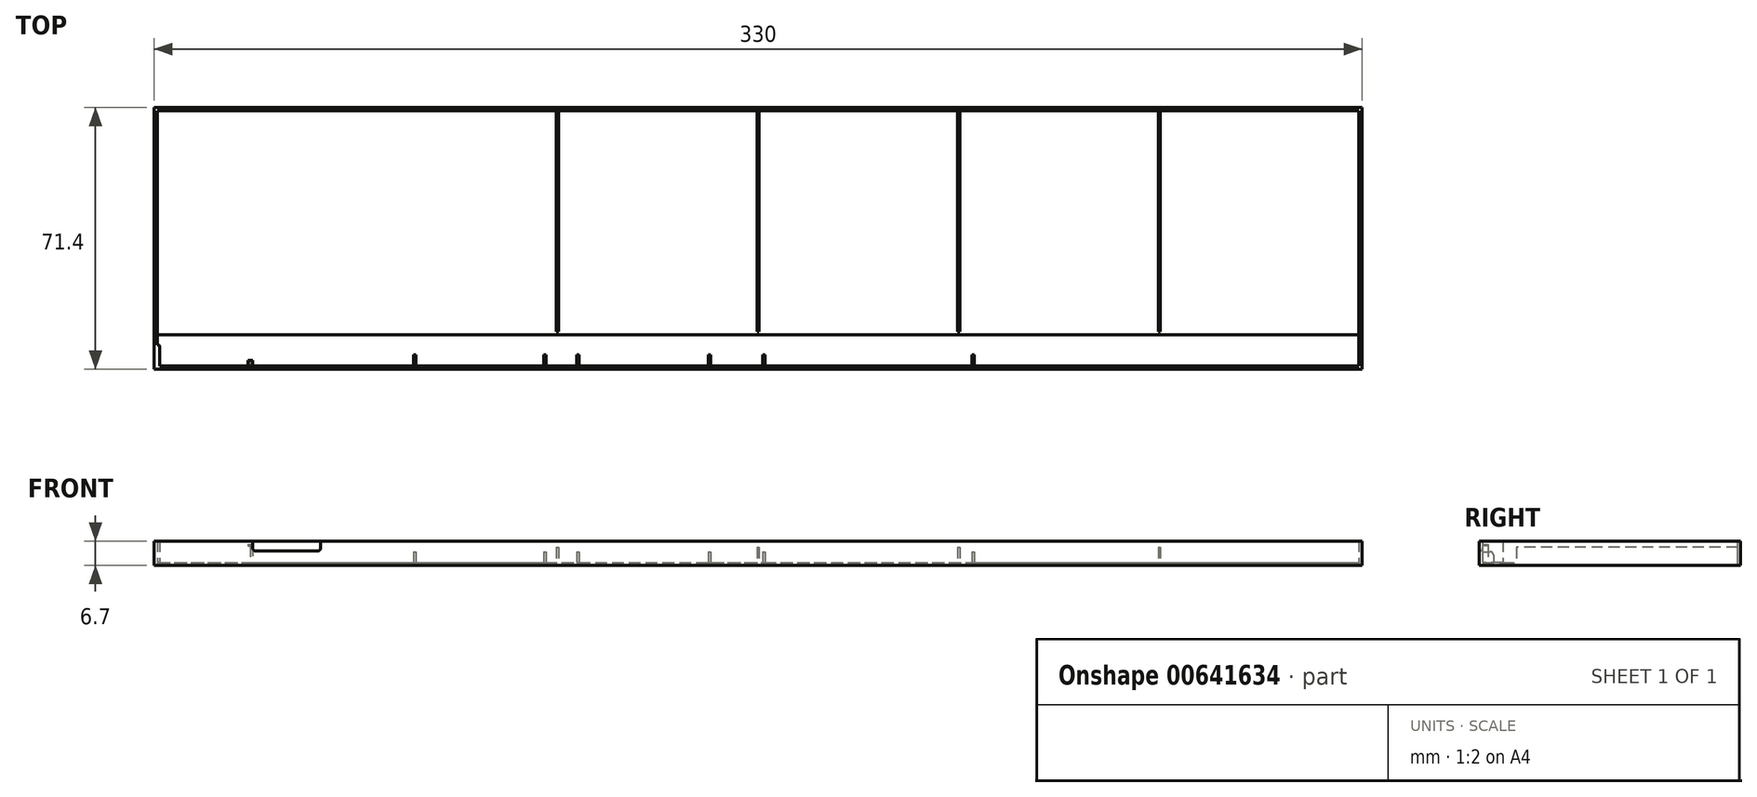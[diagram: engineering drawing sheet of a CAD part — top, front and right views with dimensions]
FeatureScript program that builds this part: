
annotation { "Feature Type Name" : "Feature", "Feature Type Description" : "" }
export const myFeature = defineFeature(function(context is Context, id is Id, definition is map)
    precondition{}
    {
        {
            var Q0;
            Q0=qCreatedBy(makeId("Top.planeOp"),FACE);
            var sketch = newSketch(context, id + "F0", { "sketchPlane" : qUnion([Q0])});
            skLineSegment(sketch, "E0.bottom", {"start": v(-165, -35.7) * mm, "end": v(165, -35.7) * mm});
            skLineSegment(sketch, "E0.top", {"start": v(-165, 35.7) * mm, "end": v(165, 35.7) * mm});
            skLineSegment(sketch, "E0.left", {"start": v(-165, -35.7) * mm, "end": v(-165, 35.7) * mm});
            skLineSegment(sketch, "E0.right", {"start": v(165, -35.7) * mm, "end": v(165, 35.7) * mm});
            skLineSegment(sketch, "E1.bottom", {"start": v(-164.1, -34.8) * mm, "end": v(164.1, -34.8) * mm});
            skLineSegment(sketch, "E1.top", {"start": v(-164.1, 34.8) * mm, "end": v(164.1, 34.8) * mm});
            skLineSegment(sketch, "E1.left", {"start": v(-164.1, -34.8) * mm, "end": v(-164.1, 34.8) * mm});
            skLineSegment(sketch, "E1.right", {"start": v(164.1, -34.8) * mm, "end": v(164.1, 34.8) * mm});
            skLineSegment(sketch, "E2", {"start": v(0, 35.7) * mm, "end": v(0, -35.7) * mm, "construction": true});
            skLineSegment(sketch, "E3", {"start": v(165, 0) * mm, "end": v(-165, 0) * mm, "construction": true});
            skPoint(sketch, "E4", {"position": v(0, 0) * mm});
            skLineSegment(sketch, "E5.bottom", {"start": v(-164.1, -26.3) * mm, "end": v(164.1, -26.3) * mm});
            skLineSegment(sketch, "E5.left", {"start": v(-164.1, -26.3) * mm, "end": v(-164.1, -34.8) * mm});
            skLineSegment(sketch, "E5.right", {"start": v(164.1, -26.3) * mm, "end": v(164.1, -34.8) * mm});
            skLineSegment(sketch, "E6.bottom", {"start": v(-109.9, 34.8) * mm, "end": v(-109.3, 34.8) * mm});
            skLineSegment(sketch, "E6.top", {"start": v(-109.9, -25.5) * mm, "end": v(-109.3, -25.5) * mm});
            skLineSegment(sketch, "E6.left", {"start": v(-109.9, 34.8) * mm, "end": v(-109.9, -25.5) * mm});
            skLineSegment(sketch, "E6.right", {"start": v(-109.3, 34.8) * mm, "end": v(-109.3, -25.5) * mm});
            skLineSegment(sketch, "E7.1.0.0", {"start": v(-55.1, 34.8) * mm, "end": v(-55.1, -25.5) * mm});
            skLineSegment(sketch, "E7.1.0.1", {"start": v(-54.5, 34.8) * mm, "end": v(-54.5, -25.5) * mm});
            skLineSegment(sketch, "E7.1.0.2", {"start": v(-55.1, -25.5) * mm, "end": v(-54.5, -25.5) * mm});
            skLineSegment(sketch, "E7.2.0.0", {"start": v(-0.3, 34.8) * mm, "end": v(-0.3, -25.5) * mm});
            skLineSegment(sketch, "E7.2.0.1", {"start": v(0.3, 34.8) * mm, "end": v(0.3, -25.5) * mm});
            skLineSegment(sketch, "E7.2.0.2", {"start": v(-0.3, -25.5) * mm, "end": v(0.3, -25.5) * mm});
            skLineSegment(sketch, "E7.3.0.0", {"start": v(54.5, 34.8) * mm, "end": v(54.5, -25.5) * mm});
            skLineSegment(sketch, "E7.3.0.1", {"start": v(55.1, 34.8) * mm, "end": v(55.1, -25.5) * mm});
            skLineSegment(sketch, "E7.3.0.2", {"start": v(54.5, -25.5) * mm, "end": v(55.1, -25.5) * mm});
            skLineSegment(sketch, "E7.4.0.0", {"start": v(109.3, 34.8) * mm, "end": v(109.3, -25.5) * mm});
            skLineSegment(sketch, "E7.4.0.1", {"start": v(109.9, 34.8) * mm, "end": v(109.9, -25.5) * mm});
            skLineSegment(sketch, "E7.4.0.2", {"start": v(109.3, -25.5) * mm, "end": v(109.9, -25.5) * mm});
            skLineSegment(sketch, "E7.direction1", {"start": v(-109.9, -25.5) * mm, "end": v(-55.1, -25.5) * mm, "construction": true});
            skLineSegment(sketch, "E8.bottom", {"start": v(-152, 26.7) * mm, "end": v(-122, 26.7) * mm});
            skLineSegment(sketch, "E8.top", {"start": v(-152, -17.3) * mm, "end": v(-122, -17.3) * mm});
            skLineSegment(sketch, "E8.left", {"start": v(-156, 22.7) * mm, "end": v(-156, -13.3) * mm});
            skLineSegment(sketch, "E8.right", {"start": v(-118, 22.7) * mm, "end": v(-118, -13.3) * mm});
            skPoint(sketch, "E9.visualSharp", {"position": v(-156, -17.3) * mm});
            skArc(sketch, "E9.filletArc", {"start": v(-156, -13.3) * mm, "mid": v(-154.83, -16.13) * mm, "end": v(-152, -17.3) * mm});
            skPoint(sketch, "E10.visualSharp", {"position": v(-118, -17.3) * mm});
            skArc(sketch, "E10.filletArc", {"start": v(-122, -17.3) * mm, "mid": v(-119.17, -16.13) * mm, "end": v(-118, -13.3) * mm});
            skPoint(sketch, "E11.visualSharp", {"position": v(-118, 26.7) * mm});
            skArc(sketch, "E11.filletArc", {"start": v(-118, 22.7) * mm, "mid": v(-119.17, 25.53) * mm, "end": v(-122, 26.7) * mm});
            skPoint(sketch, "E12.visualSharp", {"position": v(-156, 26.7) * mm});
            skArc(sketch, "E12.filletArc", {"start": v(-152, 26.7) * mm, "mid": v(-154.83, 25.53) * mm, "end": v(-156, 22.7) * mm});
            skLineSegment(sketch, "E13.1.0.0", {"start": v(-63.2, 22.7) * mm, "end": v(-63.2, -13.3) * mm});
            skLineSegment(sketch, "E13.1.0.1", {"start": v(-97.2, 26.7) * mm, "end": v(-67.2, 26.7) * mm});
            skLineSegment(sketch, "E13.1.0.2", {"start": v(-101.2, 22.7) * mm, "end": v(-101.2, -13.3) * mm});
            skArc(sketch, "E13.1.0.3", {"start": v(-97.2, 26.7) * mm, "mid": v(-100.03, 25.53) * mm, "end": v(-101.2, 22.7) * mm});
            skArc(sketch, "E13.1.0.4", {"start": v(-63.2, 22.7) * mm, "mid": v(-64.37, 25.53) * mm, "end": v(-67.2, 26.7) * mm});
            skArc(sketch, "E13.1.0.5", {"start": v(-67.2, -17.3) * mm, "mid": v(-64.37, -16.13) * mm, "end": v(-63.2, -13.3) * mm});
            skLineSegment(sketch, "E13.1.0.6", {"start": v(-97.2, -17.3) * mm, "end": v(-67.2, -17.3) * mm});
            skArc(sketch, "E13.1.0.7", {"start": v(-101.2, -13.3) * mm, "mid": v(-100.03, -16.13) * mm, "end": v(-97.2, -17.3) * mm});
            skLineSegment(sketch, "E13.2.0.0", {"start": v(-8.4, 22.7) * mm, "end": v(-8.4, -13.3) * mm});
            skLineSegment(sketch, "E13.2.0.1", {"start": v(-42.4, 26.7) * mm, "end": v(-12.4, 26.7) * mm});
            skLineSegment(sketch, "E13.2.0.2", {"start": v(-46.4, 22.7) * mm, "end": v(-46.4, -13.3) * mm});
            skArc(sketch, "E13.2.0.3", {"start": v(-42.4, 26.7) * mm, "mid": v(-45.23, 25.53) * mm, "end": v(-46.4, 22.7) * mm});
            skArc(sketch, "E13.2.0.4", {"start": v(-8.4, 22.7) * mm, "mid": v(-9.57, 25.53) * mm, "end": v(-12.4, 26.7) * mm});
            skArc(sketch, "E13.2.0.5", {"start": v(-12.4, -17.3) * mm, "mid": v(-9.57, -16.13) * mm, "end": v(-8.4, -13.3) * mm});
            skLineSegment(sketch, "E13.2.0.6", {"start": v(-42.4, -17.3) * mm, "end": v(-12.4, -17.3) * mm});
            skArc(sketch, "E13.2.0.7", {"start": v(-46.4, -13.3) * mm, "mid": v(-45.23, -16.13) * mm, "end": v(-42.4, -17.3) * mm});
            skLineSegment(sketch, "E13.3.0.0", {"start": v(46.4, 22.7) * mm, "end": v(46.4, -13.3) * mm});
            skLineSegment(sketch, "E13.3.0.1", {"start": v(12.4, 26.7) * mm, "end": v(42.4, 26.7) * mm});
            skLineSegment(sketch, "E13.3.0.2", {"start": v(8.4, 22.7) * mm, "end": v(8.4, -13.3) * mm});
            skArc(sketch, "E13.3.0.3", {"start": v(12.4, 26.7) * mm, "mid": v(9.57, 25.53) * mm, "end": v(8.4, 22.7) * mm});
            skArc(sketch, "E13.3.0.4", {"start": v(46.4, 22.7) * mm, "mid": v(45.23, 25.53) * mm, "end": v(42.4, 26.7) * mm});
            skArc(sketch, "E13.3.0.5", {"start": v(42.4, -17.3) * mm, "mid": v(45.23, -16.13) * mm, "end": v(46.4, -13.3) * mm});
            skLineSegment(sketch, "E13.3.0.6", {"start": v(12.4, -17.3) * mm, "end": v(42.4, -17.3) * mm});
            skArc(sketch, "E13.3.0.7", {"start": v(8.4, -13.3) * mm, "mid": v(9.57, -16.13) * mm, "end": v(12.4, -17.3) * mm});
            skLineSegment(sketch, "E13.4.0.0", {"start": v(101.2, 22.7) * mm, "end": v(101.2, -13.3) * mm});
            skLineSegment(sketch, "E13.4.0.1", {"start": v(67.2, 26.7) * mm, "end": v(97.2, 26.7) * mm});
            skLineSegment(sketch, "E13.4.0.2", {"start": v(63.2, 22.7) * mm, "end": v(63.2, -13.3) * mm});
            skArc(sketch, "E13.4.0.3", {"start": v(67.2, 26.7) * mm, "mid": v(64.37, 25.53) * mm, "end": v(63.2, 22.7) * mm});
            skArc(sketch, "E13.4.0.4", {"start": v(101.2, 22.7) * mm, "mid": v(100.03, 25.53) * mm, "end": v(97.2, 26.7) * mm});
            skArc(sketch, "E13.4.0.5", {"start": v(97.2, -17.3) * mm, "mid": v(100.03, -16.13) * mm, "end": v(101.2, -13.3) * mm});
            skLineSegment(sketch, "E13.4.0.6", {"start": v(67.2, -17.3) * mm, "end": v(97.2, -17.3) * mm});
            skArc(sketch, "E13.4.0.7", {"start": v(63.2, -13.3) * mm, "mid": v(64.37, -16.13) * mm, "end": v(67.2, -17.3) * mm});
            skLineSegment(sketch, "E13.5.0.0", {"start": v(156, 22.7) * mm, "end": v(156, -13.3) * mm});
            skLineSegment(sketch, "E13.5.0.1", {"start": v(122, 26.7) * mm, "end": v(152, 26.7) * mm});
            skLineSegment(sketch, "E13.5.0.2", {"start": v(118, 22.7) * mm, "end": v(118, -13.3) * mm});
            skArc(sketch, "E13.5.0.3", {"start": v(122, 26.7) * mm, "mid": v(119.17, 25.53) * mm, "end": v(118, 22.7) * mm});
            skArc(sketch, "E13.5.0.4", {"start": v(156, 22.7) * mm, "mid": v(154.83, 25.53) * mm, "end": v(152, 26.7) * mm});
            skArc(sketch, "E13.5.0.5", {"start": v(152, -17.3) * mm, "mid": v(154.83, -16.13) * mm, "end": v(156, -13.3) * mm});
            skLineSegment(sketch, "E13.5.0.6", {"start": v(122, -17.3) * mm, "end": v(152, -17.3) * mm});
            skArc(sketch, "E13.5.0.7", {"start": v(118, -13.3) * mm, "mid": v(119.17, -16.13) * mm, "end": v(122, -17.3) * mm});
            skLineSegment(sketch, "E13.direction1", {"start": v(-118, -13.3) * mm, "end": v(-63.2, -13.3) * mm, "construction": true});
            skSolve(sketch);
        }
        {
            var Q0;
            {var subQ1=sQuery(id+"F0.wireOp",EDGE,"E1.left");Q0=makeQuery(id+"F0.imprint","IMPRINT",FACE,{"disambiguationData":[TD([[makeQuery(id+"F0.imprint","IMPRINT",EDGE,{"derivedFrom":subQ1}),-1.0]])]});}
            extrude(context, id + "F1", {"entities" : qUnion([Q0]), "depth" : .5 * mm, "offsetDistance" : 25 * mm});
        }
        {
            var Q0;
            Q0=makeQuery(id+"F0.imprint","IMPRINT",FACE,{"disambiguationData":[TD([[makeQuery(id+"F0.imprint","IMPRINT",EDGE,{"derivedFrom":sQuery(id+"F0.wireOp",EDGE,"E5.bottom")}),-1.0]])]});
            extrude(context, id + "F2", {"entities" : qUnion([Q0]), "operationType" : NewBodyOperationType.ADD, "depth" : .8 * mm, "offsetDistance" : 25 * mm});
        }
        {
            var Q0;
            Q0=makeQuery(id+"F0.imprint","IMPRINT",FACE,{"disambiguationData":[TD([[makeQuery(id+"F0.imprint","IMPRINT",EDGE,{"derivedFrom":sQuery(id+"F0.wireOp",EDGE,"E0.bottom")}),1.0]])]});
            extrude(context, id + "F3", {"entities" : qUnion([Q0]), "operationType" : NewBodyOperationType.ADD, "depth" : 6.7 * mm, "offsetDistance" : 25 * mm});
        }
        {
            var Q0;
            Q0=makeQuery(id+"F0.imprint","IMPRINT",FACE,{"disambiguationData":[TD([[makeQuery(id+"F0.imprint","IMPRINT",EDGE,{"derivedFrom":sQuery(id+"F0.wireOp",EDGE,"E6.bottom")}),-1.0]])]});
            var Q1;
            {var subQ0=sQuery(id+"F0.wireOp",EDGE,"E7.1.0.0");Q1=makeQuery(id+"F0.imprint","IMPRINT",FACE,{"disambiguationData":[TD([[makeQuery(id+"F0.imprint","IMPRINT",EDGE,{"derivedFrom":subQ0}),1.0]])]});}
            var Q2;
            {var subQ0=sQuery(id+"F0.wireOp",EDGE,"E7.2.0.0");Q2=makeQuery(id+"F0.imprint","IMPRINT",FACE,{"disambiguationData":[TD([[makeQuery(id+"F0.imprint","IMPRINT",EDGE,{"derivedFrom":subQ0}),1.0]])]});}
            var Q3;
            {var subQ0=sQuery(id+"F0.wireOp",EDGE,"E7.3.0.0");Q3=makeQuery(id+"F0.imprint","IMPRINT",FACE,{"disambiguationData":[TD([[makeQuery(id+"F0.imprint","IMPRINT",EDGE,{"derivedFrom":subQ0}),1.0]])]});}
            var Q4;
            {var subQ0=sQuery(id+"F0.wireOp",EDGE,"E7.4.0.0");Q4=makeQuery(id+"F0.imprint","IMPRINT",FACE,{"disambiguationData":[TD([[makeQuery(id+"F0.imprint","IMPRINT",EDGE,{"derivedFrom":subQ0}),1.0]])]});}
            extrude(context, id + "F4", {"entities" : qUnion([Q0, Q1, Q2, Q3, Q4]), "operationType" : NewBodyOperationType.ADD, "depth" : 5 * mm, "offsetDistance" : 25 * mm});
        }
        {
            var Q0;
            Q0=makeQuery(id+"F2.opExtrude","CAP_FACE",FACE,{"disambiguationData":[OSD([sQuery(id+"F0.wireOp",EDGE,"E5.bottom"),sQuery(id+"F0.wireOp",EDGE,"E1.bottom"),sQuery(id+"F0.wireOp",EDGE,"E5.left"),sQuery(id+"F0.wireOp",EDGE,"E5.right")])],"isStart":false});
            var sketch = newSketch(context, id + "F5", { "sketchPlane" : qUnion([Q0])});
            skLineSegment(sketch, "E14.bottom", {"start": v(-164.1, -29.2) * mm, "end": v(-163.68, -29.2) * mm});
            skLineSegment(sketch, "E14.top", {"start": v(-164.1, -34.8) * mm, "end": v(-163.5, -34.8) * mm});
            skLineSegment(sketch, "E14.left", {"start": v(-164.1, -29.2) * mm, "end": v(-164.1, -34.8) * mm});
            skLineSegment(sketch, "E14.right", {"start": v(-163.5, -29.38) * mm, "end": v(-163.5, -34.8) * mm});
            skPoint(sketch, "E15.visualSharp", {"position": v(-163.5, -29.2) * mm});
            skArc(sketch, "E15.filletArc", {"start": v(-163.5, -29.38) * mm, "mid": v(-163.55, -29.25) * mm, "end": v(-163.68, -29.2) * mm});
            skSolve(sketch);
        }
        {
            var Q0;
            Q0=makeQuery(id+"F5.imprint","IMPRINT",FACE,{"disambiguationData":[TD([[makeQuery(id+"F5.imprint","IMPRINT",EDGE,{"derivedFrom":sQuery(id+"F5.wireOp",EDGE,"E14.bottom")}),-1.0]])]});
            var Q1;
            Q1=makeQuery(id+"F3.opExtrude","CAP_FACE",FACE,{"disambiguationData":[OSD([sQuery(id+"F0.wireOp",EDGE,"E0.bottom"),sQuery(id+"F0.wireOp",EDGE,"E0.top"),sQuery(id+"F0.wireOp",EDGE,"E0.left"),sQuery(id+"F0.wireOp",EDGE,"E0.right"),sQuery(id+"F0.wireOp",EDGE,"E1.top"),sQuery(id+"F0.wireOp",EDGE,"E1.left"),sQuery(id+"F0.wireOp",EDGE,"E1.right"),sQuery(id+"F0.wireOp",EDGE,"E1.bottom"),sQuery(id+"F0.wireOp",EDGE,"E5.left"),sQuery(id+"F0.wireOp",EDGE,"E5.right"),sQuery(id+"F0.wireOp",EDGE,"E6.bottom")])],"isStart":false});
            extrude(context, id + "F6", {"entities" : qUnion([Q0]), "operationType" : NewBodyOperationType.ADD, "endBound" : BoundingType.UP_TO_SURFACE, "depth" : 25 * mm, "endBoundEntityFace" : qUnion([Q1]), "offsetDistance" : 25 * mm});
        }
        {
            var Q0;
            Q0=makeQuery(id+"F3.opExtrude","SWEPT_FACE",FACE,{"disambiguationData":[OSD([sQuery(id+"F0.wireOp",EDGE,"E0.bottom")])]});
            var sketch = newSketch(context, id + "F7", { "sketchPlane" : qUnion([Q0])});
            skLineSegment(sketch, "E16.bottom", {"start": v(-138, 6.7) * mm, "end": v(-119.5, 6.7) * mm});
            skLineSegment(sketch, "E16.top", {"start": v(-138, 4) * mm, "end": v(-119.5, 4) * mm});
            skLineSegment(sketch, "E16.left", {"start": v(-138, 6.7) * mm, "end": v(-138, 4) * mm});
            skLineSegment(sketch, "E16.right", {"start": v(-119.5, 6.7) * mm, "end": v(-119.5, 4) * mm});
            skSolve(sketch);
        }
        {
            var Q0;
            Q0=makeQuery(id+"F7.imprint","IMPRINT",FACE,{"disambiguationData":[TD([[makeQuery(id+"F7.imprint","IMPRINT",EDGE,{"derivedFrom":sQuery(id+"F7.wireOp",EDGE,"E16.bottom")}),-1.0]])]});
            extrude(context, id + "F8", {"entities" : qUnion([Q0]), "operationType" : NewBodyOperationType.REMOVE, "endBound" : BoundingType.UP_TO_NEXT, "oppositeDirection" : true, "depth" : 25 * mm, "offsetDistance" : 25 * mm});
        }
        {
            var Q0;
            Q0=makeQuery(id+"F8.boolean.opBoolean","COPY",EDGE,{"derivedFrom":makeQuery(id+"F8.opExtrude","SWEPT_EDGE",EDGE,{"disambiguationData":[OSD([sQuery(id+"F0.wireOp",EDGE,"E0.bottom"),sQuery(id+"F7.wireOp",EDGE,"E16.bottom"),sQuery(id+"F7.wireOp",EDGE,"E16.left")])]})});
            var Q1;
            Q1=makeQuery(id+"F8.boolean.opBoolean","COPY",EDGE,{"derivedFrom":makeQuery(id+"F8.opExtrude","SWEPT_EDGE",EDGE,{"disambiguationData":[OSD([sQuery(id+"F0.wireOp",EDGE,"E0.bottom"),sQuery(id+"F7.wireOp",EDGE,"E16.bottom"),sQuery(id+"F7.wireOp",EDGE,"E16.right")])]})});
            var Q2;
            Q2=makeQuery(id+"F8.boolean.opBoolean","COPY",EDGE,{"derivedFrom":makeQuery(id+"F8.opExtrude","SWEPT_EDGE",EDGE,{"disambiguationData":[OSD([sQuery(id+"F7.wireOp",EDGE,"E16.top"),sQuery(id+"F7.wireOp",EDGE,"E16.left")])]})});
            var Q3;
            Q3=makeQuery(id+"F8.boolean.opBoolean","COPY",EDGE,{"derivedFrom":makeQuery(id+"F8.opExtrude","SWEPT_EDGE",EDGE,{"disambiguationData":[OSD([sQuery(id+"F7.wireOp",EDGE,"E16.top"),sQuery(id+"F7.wireOp",EDGE,"E16.right")])]})});
            fillet(context, id + "F9", {"entities" : qUnion([Q0, Q1, Q2, Q3]), "radius" : .75 * mm, "tangentPropagation" : true, "allowEdgeOverflow" : false});
        }
        {
            var Q0;
            Q0=makeQuery(id+"F2.opExtrude","CAP_FACE",FACE,{"disambiguationData":[OSD([sQuery(id+"F0.wireOp",EDGE,"E5.bottom"),sQuery(id+"F0.wireOp",EDGE,"E1.bottom"),sQuery(id+"F0.wireOp",EDGE,"E5.left"),sQuery(id+"F0.wireOp",EDGE,"E5.right")])],"isStart":false});
            var sketch = newSketch(context, id + "F10", { "sketchPlane" : qUnion([Q0])});
            skLineSegment(sketch, "E17.bottom", {"start": v(-138.7, -34.8) * mm, "end": v(-138.1, -34.8) * mm});
            skLineSegment(sketch, "E17.top", {"start": v(-138.7, -33.3) * mm, "end": v(-138.1, -33.3) * mm});
            skLineSegment(sketch, "E17.left", {"start": v(-138.7, -34.8) * mm, "end": v(-138.7, -33.3) * mm});
            skLineSegment(sketch, "E17.right", {"start": v(-138.1, -34.8) * mm, "end": v(-138.1, -33.3) * mm});
            skLineSegment(sketch, "E18.bottom", {"start": v(-94.1, -34.8) * mm, "end": v(-93.5, -34.8) * mm});
            skLineSegment(sketch, "E18.top", {"start": v(-94.1, -31.8) * mm, "end": v(-93.5, -31.8) * mm});
            skLineSegment(sketch, "E18.left", {"start": v(-94.1, -34.8) * mm, "end": v(-94.1, -31.8) * mm});
            skLineSegment(sketch, "E18.right", {"start": v(-93.5, -34.8) * mm, "end": v(-93.5, -31.8) * mm});
            skLineSegment(sketch, "E19.bottom", {"start": v(-58.5, -34.8) * mm, "end": v(-57.9, -34.8) * mm});
            skLineSegment(sketch, "E19.top", {"start": v(-58.5, -31.8) * mm, "end": v(-57.9, -31.8) * mm});
            skLineSegment(sketch, "E19.left", {"start": v(-58.5, -34.8) * mm, "end": v(-58.5, -31.8) * mm});
            skLineSegment(sketch, "E19.right", {"start": v(-57.9, -34.8) * mm, "end": v(-57.9, -31.8) * mm});
            skLineSegment(sketch, "E20.bottom", {"start": v(-49.5, -34.8) * mm, "end": v(-48.9, -34.8) * mm});
            skLineSegment(sketch, "E20.top", {"start": v(-49.5, -31.8) * mm, "end": v(-48.9, -31.8) * mm});
            skLineSegment(sketch, "E20.left", {"start": v(-49.5, -34.8) * mm, "end": v(-49.5, -31.8) * mm});
            skLineSegment(sketch, "E20.right", {"start": v(-48.9, -34.8) * mm, "end": v(-48.9, -31.8) * mm});
            skLineSegment(sketch, "E21.bottom", {"start": v(-13.6, -34.8) * mm, "end": v(-13, -34.8) * mm});
            skLineSegment(sketch, "E21.top", {"start": v(-13.6, -31.8) * mm, "end": v(-13, -31.8) * mm});
            skLineSegment(sketch, "E21.left", {"start": v(-13.6, -34.8) * mm, "end": v(-13.6, -31.8) * mm});
            skLineSegment(sketch, "E21.right", {"start": v(-13, -34.8) * mm, "end": v(-13, -31.8) * mm});
            skLineSegment(sketch, "E22.bottom", {"start": v(1.3, -34.8) * mm, "end": v(1.9, -34.8) * mm});
            skLineSegment(sketch, "E22.top", {"start": v(1.3, -31.8) * mm, "end": v(1.9, -31.8) * mm});
            skLineSegment(sketch, "E22.left", {"start": v(1.3, -34.8) * mm, "end": v(1.3, -31.8) * mm});
            skLineSegment(sketch, "E22.right", {"start": v(1.9, -34.8) * mm, "end": v(1.9, -31.8) * mm});
            skLineSegment(sketch, "E23.bottom", {"start": v(58.4, -34.8) * mm, "end": v(59, -34.8) * mm});
            skLineSegment(sketch, "E23.top", {"start": v(58.4, -31.8) * mm, "end": v(59, -31.8) * mm});
            skLineSegment(sketch, "E23.left", {"start": v(58.4, -34.8) * mm, "end": v(58.4, -31.8) * mm});
            skLineSegment(sketch, "E23.right", {"start": v(59, -34.8) * mm, "end": v(59, -31.8) * mm});
            skSolve(sketch);
        }
        {
            var Q0;
            Q0=makeQuery(id+"F10.imprint","IMPRINT",FACE,{"disambiguationData":[TD([[makeQuery(id+"F10.imprint","IMPRINT",EDGE,{"derivedFrom":sQuery(id+"F10.wireOp",EDGE,"E17.bottom")}),1.0]])]});
            extrude(context, id + "F11", {"entities" : qUnion([Q0]), "operationType" : NewBodyOperationType.ADD, "depth" : 5 * mm, "offsetDistance" : 25 * mm});
        }
        {
            var Q0;
            Q0=makeQuery(id+"F10.imprint","IMPRINT",FACE,{"disambiguationData":[TD([[makeQuery(id+"F10.imprint","IMPRINT",EDGE,{"derivedFrom":sQuery(id+"F10.wireOp",EDGE,"E18.bottom")}),1.0]])]});
            var Q1;
            Q1=makeQuery(id+"F10.imprint","IMPRINT",FACE,{"disambiguationData":[TD([[makeQuery(id+"F10.imprint","IMPRINT",EDGE,{"derivedFrom":sQuery(id+"F10.wireOp",EDGE,"E19.bottom")}),1.0]])]});
            var Q2;
            Q2=makeQuery(id+"F10.imprint","IMPRINT",FACE,{"disambiguationData":[TD([[makeQuery(id+"F10.imprint","IMPRINT",EDGE,{"derivedFrom":sQuery(id+"F10.wireOp",EDGE,"E20.bottom")}),1.0]])]});
            var Q3;
            Q3=makeQuery(id+"F10.imprint","IMPRINT",FACE,{"disambiguationData":[TD([[makeQuery(id+"F10.imprint","IMPRINT",EDGE,{"derivedFrom":sQuery(id+"F10.wireOp",EDGE,"E21.bottom")}),1.0]])]});
            var Q4;
            Q4=makeQuery(id+"F10.imprint","IMPRINT",FACE,{"disambiguationData":[TD([[makeQuery(id+"F10.imprint","IMPRINT",EDGE,{"derivedFrom":sQuery(id+"F10.wireOp",EDGE,"E22.bottom")}),1.0]])]});
            var Q5;
            Q5=makeQuery(id+"F10.imprint","IMPRINT",FACE,{"disambiguationData":[TD([[makeQuery(id+"F10.imprint","IMPRINT",EDGE,{"derivedFrom":sQuery(id+"F10.wireOp",EDGE,"E23.bottom")}),1.0]])]});
            extrude(context, id + "F12", {"entities" : qUnion([Q0, Q1, Q2, Q3, Q4, Q5]), "operationType" : NewBodyOperationType.ADD, "depth" : 3 * mm, "offsetDistance" : 25 * mm});
        }
        {
            var Q0;
            Q0=makeQuery(id+"F12.opExtrude","CAP_EDGE",EDGE,{"disambiguationData":[OSD([sQuery(id+"F10.wireOp",EDGE,"E23.top")])],"isStart":false});
            var Q1;
            Q1=makeQuery(id+"F12.opExtrude","CAP_EDGE",EDGE,{"disambiguationData":[OSD([sQuery(id+"F10.wireOp",EDGE,"E22.top")])],"isStart":false});
            var Q2;
            Q2=makeQuery(id+"F12.opExtrude","CAP_EDGE",EDGE,{"disambiguationData":[OSD([sQuery(id+"F10.wireOp",EDGE,"E21.top")])],"isStart":false});
            var Q3;
            Q3=makeQuery(id+"F12.opExtrude","CAP_EDGE",EDGE,{"disambiguationData":[OSD([sQuery(id+"F10.wireOp",EDGE,"E20.top")])],"isStart":false});
            var Q4;
            Q4=makeQuery(id+"F12.opExtrude","CAP_EDGE",EDGE,{"disambiguationData":[OSD([sQuery(id+"F10.wireOp",EDGE,"E19.top")])],"isStart":false});
            var Q5;
            Q5=makeQuery(id+"F12.opExtrude","CAP_EDGE",EDGE,{"disambiguationData":[OSD([sQuery(id+"F10.wireOp",EDGE,"E18.top")])],"isStart":false});
            fillet(context, id + "F13", {"entities" : qUnion([Q0, Q1, Q2, Q3, Q4, Q5]), "radius" : 1 * mm, "tangentPropagation" : true, "allowEdgeOverflow" : false});
        }
        {
            var Q0;
            Q0=makeQuery(id+"F11.opExtrude","SWEPT_FACE",FACE,{"disambiguationData":[OSD([sQuery(id+"F10.wireOp",EDGE,"E17.left")])]});
            var sketch = newSketch(context, id + "F14", { "sketchPlane" : qUnion([Q0])});
            skLineSegment(sketch, "E24.bottom", {"start": v(33.3, 5.8) * mm, "end": v(34.8, 5.8) * mm});
            skLineSegment(sketch, "E24.top", {"start": v(33.3, 5.4) * mm, "end": v(34.8, 5.4) * mm});
            skLineSegment(sketch, "E24.left", {"start": v(33.3, 5.8) * mm, "end": v(33.3, 5.4) * mm});
            skLineSegment(sketch, "E24.right", {"start": v(34.8, 5.8) * mm, "end": v(34.8, 5.4) * mm});
            skSolve(sketch);
        }
        {
            var Q0;
            Q0=makeQuery(id+"F14.imprint","IMPRINT",FACE,{"disambiguationData":[TD([[makeQuery(id+"F14.imprint","IMPRINT",EDGE,{"derivedFrom":sQuery(id+"F14.wireOp",EDGE,"E24.bottom")}),1.0]])]});
            extrude(context, id + "F15", {"entities" : qUnion([Q0]), "operationType" : NewBodyOperationType.ADD, "depth" : .6 * mm, "offsetDistance" : 25 * mm});
        }
        {
            var Q0;
            Q0=makeQuery(id+"F11.opExtrude","CAP_EDGE",EDGE,{"disambiguationData":[OSD([sQuery(id+"F10.wireOp",EDGE,"E17.right")])],"isStart":false});
            fillet(context, id + "F16", {"entities" : qUnion([Q0]), "radius" : .25 * mm, "tangentPropagation" : true, "allowEdgeOverflow" : false});
        }
    });
